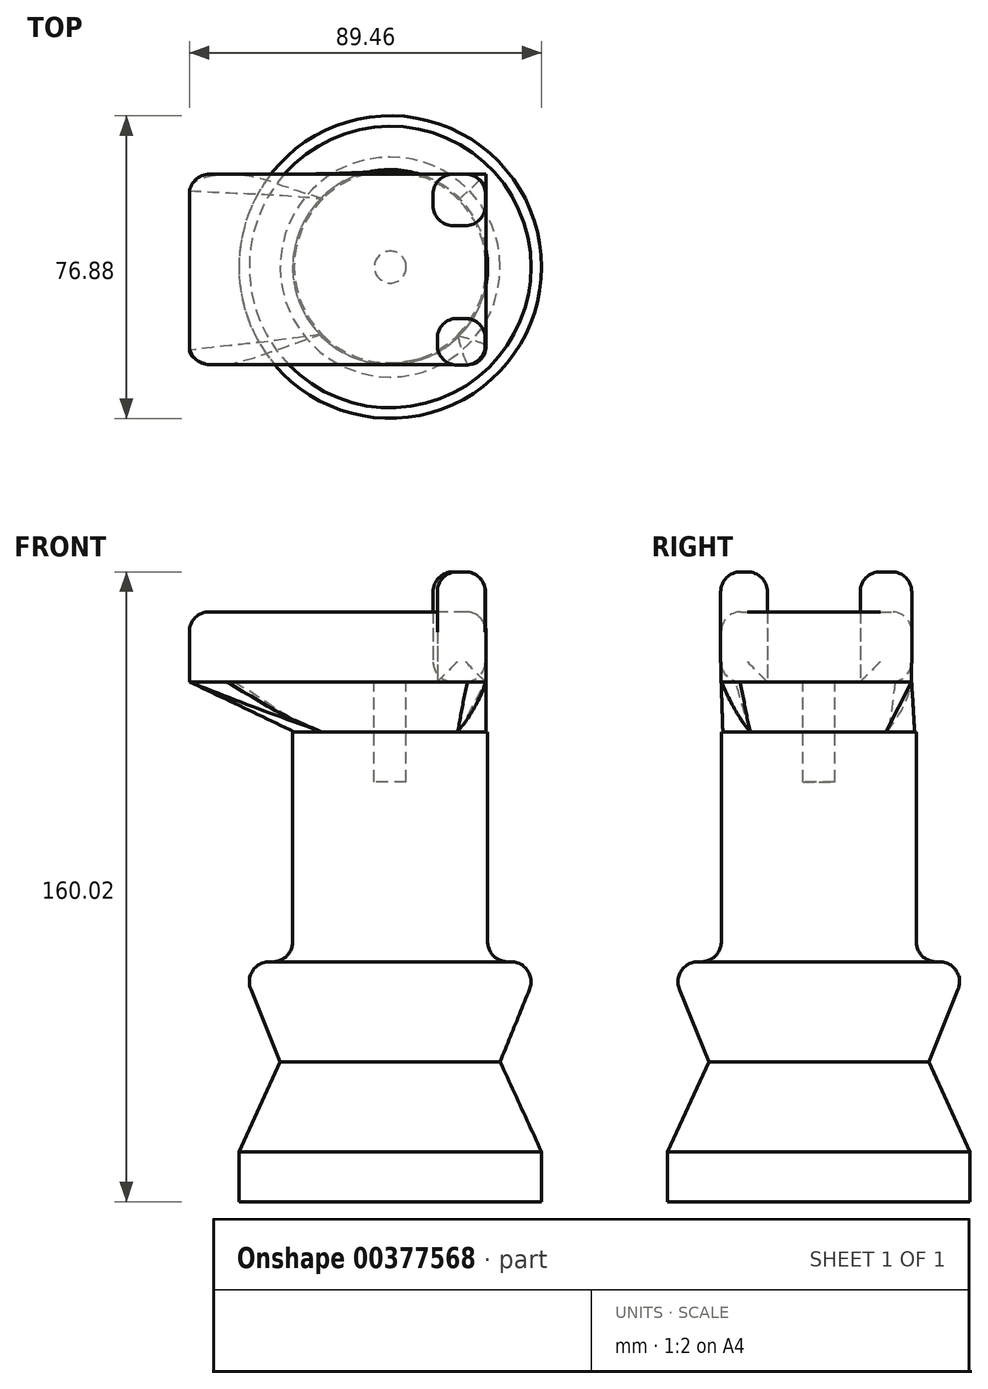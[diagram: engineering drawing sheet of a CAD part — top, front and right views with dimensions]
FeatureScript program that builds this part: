
annotation { "Feature Type Name" : "Feature", "Feature Type Description" : "" }
export const myFeature = defineFeature(function(context is Context, id is Id, definition is map)
    precondition{}
    {
        {
            var Q0;
            Q0=qCreatedBy(makeId("Top.planeOp"),FACE);
            var sketch = newSketch(context, id + "F0", { "sketchPlane" : qUnion([Q0])});
            skCircle(sketch, "E0", {"center": v(0, 0) * mm, "radius": 38.44 * mm});
            skSolve(sketch);
        }
        {
            var Q0;
            Q0=makeQuery(id+"F0.imprint","IMPRINT",FACE,{"disambiguationData":[TD([[makeQuery(id+"F0.imprint","IMPRINT",EDGE,{"derivedFrom":sQuery(id+"F0.wireOp",EDGE,"E0")}),1.0]])]});
            extrude(context, id + "F1", {"entities" : qUnion([Q0]), "oppositeDirection" : true, "depth" : 12.7 * mm});
        }
        {
            var Q0;
            Q0=qCreatedBy(makeId("Top.planeOp"),FACE);
            cPlane(context, id + "F2", {"entities" : qUnion([Q0]), "cplaneType" : CPlaneType.OFFSET, "offset" : 22.86 * mm, "width" : 152.4 * mm, "height" : 152.4 * mm});
        }
        {
            var Q0;
            Q0=qCreatedBy(id+"F2.planeOp",FACE);
            var sketch = newSketch(context, id + "F3", { "sketchPlane" : qUnion([Q0])});
            skCircle(sketch, "E1", {"center": v(0, 0) * mm, "radius": 27.93 * mm});
            skSolve(sketch);
        }
        {
            var Q1;
            Q1=makeQuery(id+"F0.imprint","IMPRINT",FACE,{"disambiguationData":[TD([[makeQuery(id+"F0.imprint","IMPRINT",EDGE,{"derivedFrom":sQuery(id+"F0.wireOp",EDGE,"E0")}),1.0]])]});
            var Q2;
            Q2=makeQuery(id+"F3.imprint","IMPRINT",FACE,{"disambiguationData":[TD([[makeQuery(id+"F3.imprint","IMPRINT",EDGE,{"derivedFrom":sQuery(id+"F3.wireOp",EDGE,"E1")}),1.0]])]});
            loft(context, id + "F4", {"operationType" : NewBodyOperationType.ADD, "sheetProfilesArray" : [{ "sheetProfileEntities" : qUnion([Q1]) }, { "sheetProfileEntities" : qUnion([Q2]) }]});
        }
        {
            var Q0;
            Q0=qCreatedBy(id+"F2.planeOp",FACE);
            cPlane(context, id + "F5", {"entities" : qUnion([Q0]), "cplaneType" : CPlaneType.OFFSET, "offset" : 25.4 * mm, "width" : 152.4 * mm, "height" : 152.4 * mm});
        }
        {
            var Q0;
            Q0=qCreatedBy(id+"F5.planeOp",FACE);
            var sketch = newSketch(context, id + "F6", { "sketchPlane" : qUnion([Q0])});
            skCircle(sketch, "E2", {"center": v(0, 0) * mm, "radius": 38.24 * mm});
            skSolve(sketch);
        }
        {
            var Q1;
            Q1 = qSketchRegion(id + "F6", true);
            var Q2;
            Q2=makeQuery(id+"F4.opLoft","CAP_FACE",FACE,{"disambiguationData":[OSD([makeQuery(id+"F3.imprint","IMPRINT",FACE,{"disambiguationData":[TD([[makeQuery(id+"F3.imprint","IMPRINT",EDGE,{"derivedFrom":sQuery(id+"F3.wireOp",EDGE,"E1")}),1.0]])]})])],"isStart":true});
            loft(context, id + "F7", {"operationType" : NewBodyOperationType.ADD, "sheetProfilesArray" : [{ "sheetProfileEntities" : qUnion([Q1]) }, { "sheetProfileEntities" : qUnion([Q2]) }]});
        }
        {
            var Q0;
            Q0=makeQuery(id+"F6.imprint","IMPRINT",FACE,{"disambiguationData":[TD([[makeQuery(id+"F6.imprint","IMPRINT",EDGE,{"derivedFrom":sQuery(id+"F6.wireOp",EDGE,"E2")}),1.0]])]});
            var sketch = newSketch(context, id + "F8", { "sketchPlane" : qUnion([Q0])});
            skCircle(sketch, "E3", {"center": v(0, 0) * mm, "radius": 24.77 * mm});
            skSolve(sketch);
        }
        {
            var Q0;
            Q0 = qSketchRegion(id + "F8", true);
            extrude(context, id + "F9", {"entities" : qUnion([Q0]), "operationType" : NewBodyOperationType.ADD, "depth" : 58.42 * mm});
        }
        {
            var Q0;
            Q0=qCreatedBy(id+"F5.planeOp",FACE);
            cPlane(context, id + "F10", {"entities" : qUnion([Q0]), "cplaneType" : CPlaneType.OFFSET, "offset" : 58.42 * mm, "width" : 152.4 * mm, "height" : 152.4 * mm});
        }
        {
            var Q0;
            Q0=makeQuery(id+"F9.opExtrude","CAP_FACE",FACE,{"disambiguationData":[OSD([sQuery(id+"F8.wireOp",EDGE,"E3")])],"isStart":false});
            var sketch = newSketch(context, id + "F11", { "sketchPlane" : qUnion([Q0])});
            skCircle(sketch, "E4", {"center": v(0, 0) * mm, "radius": 24.37 * mm});
            skSolve(sketch);
        }
        {
            var Q0;
            Q0=qCreatedBy(id+"F10.planeOp",FACE);
            cPlane(context, id + "F12", {"entities" : qUnion([Q0]), "cplaneType" : CPlaneType.OFFSET, "offset" : 12.7 * mm, "width" : 152.4 * mm, "height" : 152.4 * mm});
        }
        {
            var Q0;
            Q0=qCreatedBy(id+"F12.planeOp",FACE);
            var sketch = newSketch(context, id + "F13", { "sketchPlane" : qUnion([Q0])});
            skCircle(sketch, "E5", {"center": v(0, 0) * mm, "radius": 4.05 * mm});
            skSolve(sketch);
        }
        {
            var Q0;
            Q0=makeQuery(id+"F13.imprint","IMPRINT",FACE,{"disambiguationData":[TD([[makeQuery(id+"F13.imprint","IMPRINT",EDGE,{"derivedFrom":sQuery(id+"F13.wireOp",EDGE,"E5")}),1.0]])]});
            extrude(context, id + "F14", {"entities" : qUnion([Q0]), "oppositeDirection" : true, "depth" : 25.4 * mm});
        }
        {
            var Q0;
            Q0=qCreatedBy(id+"F12.planeOp",FACE);
            var sketch = newSketch(context, id + "F15", { "sketchPlane" : qUnion([Q0])});
            skLineSegment(sketch, "E6.bottom", {"start": v(24.35, -24.8) * mm, "end": v(-51.02, -24.8) * mm});
            skLineSegment(sketch, "E6.top", {"start": v(24.35, 23.59) * mm, "end": v(-51.02, 23.59) * mm});
            skLineSegment(sketch, "E6.left", {"start": v(24.35, -24.8) * mm, "end": v(24.35, 23.59) * mm});
            skLineSegment(sketch, "E6.right", {"start": v(-51.02, -24.8) * mm, "end": v(-51.02, 23.59) * mm});
            skSolve(sketch);
        }
        {
            var Q0;
            Q0 = qSketchRegion(id + "F11", true);
            var Q1;
            Q1 = qSketchRegion(id + "F15", true);
            loft(context, id + "F16", {"sheetProfilesArray" : [{ "sheetProfileEntities" : qUnion([Q0]) }, { "sheetProfileEntities" : qUnion([Q1]) }]});
        }
        {
            var Q0;
            Q0=makeQuery(id+"F15.imprint","IMPRINT",FACE,{"disambiguationData":[TD([[makeQuery(id+"F15.imprint","IMPRINT",EDGE,{"derivedFrom":sQuery(id+"F15.wireOp",EDGE,"E6.bottom")}),-1.0]])]});
            extrude(context, id + "F17", {"entities" : qUnion([Q0]), "depth" : 17.78 * mm});
        }
        {
            var Q0;
            Q0=qCreatedBy(id+"F12.planeOp",FACE);
            cPlane(context, id + "F18", {"entities" : qUnion([Q0]), "cplaneType" : CPlaneType.OFFSET, "offset" : 7.62 * mm, "width" : 152.4 * mm, "height" : 152.4 * mm});
        }
        {
            var Q0;
            Q0=qCreatedBy(id+"F18.planeOp",FACE);
            cPlane(context, id + "F19", {"entities" : qUnion([Q0]), "cplaneType" : CPlaneType.OFFSET, "offset" : 2.54 * mm, "width" : 152.4 * mm, "height" : 152.4 * mm});
        }
        {
            var Q0;
            Q0 = qSketchRegion(id + "F13", true);
            var sketch = newSketch(context, id + "F20", { "sketchPlane" : qUnion([Q0])});
            skLineSegment(sketch, "E7.bottom", {"start": v(24.14, -24.91) * mm, "end": v(11.96, -24.91) * mm});
            skLineSegment(sketch, "E7.top", {"start": v(24.14, -13.06) * mm, "end": v(11.96, -13.06) * mm});
            skLineSegment(sketch, "E7.left", {"start": v(24.14, -24.91) * mm, "end": v(24.14, -13.06) * mm});
            skLineSegment(sketch, "E7.right", {"start": v(11.96, -24.91) * mm, "end": v(11.96, -13.06) * mm});
            skLineSegment(sketch, "E8.bottom", {"start": v(24.22, 23.61) * mm, "end": v(10.91, 23.61) * mm});
            skLineSegment(sketch, "E8.top", {"start": v(24.22, 10.53) * mm, "end": v(10.91, 10.53) * mm});
            skLineSegment(sketch, "E8.left", {"start": v(24.22, 23.61) * mm, "end": v(24.22, 10.53) * mm});
            skLineSegment(sketch, "E8.right", {"start": v(10.91, 23.61) * mm, "end": v(10.91, 10.53) * mm});
            skLineSegment(sketch, "E9.bottom", {"start": v(11.96, -13.06) * mm, "end": v(24.14, -13.06) * mm});
            skLineSegment(sketch, "E9.top", {"start": v(11.96, -13.06) * mm, "end": v(24.14, -13.06) * mm});
            skLineSegment(sketch, "E9.left", {"start": v(11.96, -13.06) * mm, "end": v(11.96, -13.06) * mm});
            skLineSegment(sketch, "E9.right", {"start": v(24.14, -13.06) * mm, "end": v(24.14, -13.06) * mm});
            skSolve(sketch);
        }
        {
            var Q0;
            Q0 = qSketchRegion(id + "F20", true);
            extrude(context, id + "F21", {"entities" : qUnion([Q0]), "depth" : 27.94 * mm});
        }
        {
            var Q0;
            Q0=makeQuery(id+"F17.opExtrude","SWEPT_EDGE",EDGE,{"disambiguationData":[OSD([sQuery(id+"F15.wireOp",EDGE,"E6.top"),sQuery(id+"F15.wireOp",EDGE,"E6.right")])]});
            fillet(context, id + "F22", {"entities" : qUnion([Q0]), "radius" : 5.08 * mm, "tangentPropagation" : true, "allowEdgeOverflow" : false});
        }
        {
            var Q0;
            Q0=makeQuery(id+"F17.opExtrude","SWEPT_EDGE",EDGE,{"disambiguationData":[OSD([sQuery(id+"F15.wireOp",EDGE,"E6.bottom"),sQuery(id+"F15.wireOp",EDGE,"E6.right")])]});
            var Q1;
            Q1=makeQuery(id+"F16.opLoft","SWEPT_EDGE",EDGE,{"disambiguationData":[OSD([sQuery(id+"F11.wireOp",EDGE,"E4"),sQuery(id+"F15.wireOp",EDGE,"E6.bottom"),sQuery(id+"F15.wireOp",EDGE,"E6.top"),sQuery(id+"F15.wireOp",EDGE,"E6.right")])]});
            var Q2;
            Q2=makeQuery(id+"F16.opLoft","SWEPT_EDGE",EDGE,{"disambiguationData":[OSD([sQuery(id+"F11.wireOp",EDGE,"E4"),sQuery(id+"F15.wireOp",EDGE,"E6.top"),sQuery(id+"F15.wireOp",EDGE,"E6.left"),sQuery(id+"F15.wireOp",EDGE,"E6.right")])]});
            fillet(context, id + "F23", {"entities" : qUnion([Q0, Q1, Q2]), "radius" : 5.08 * mm, "tangentPropagation" : true, "allowEdgeOverflow" : false});
        }
        {
            var Q0;
            Q0=makeQuery(id+"F7.opLoft","CAP_FACE",FACE,{"disambiguationData":[OSD([makeQuery(id+"F6.imprint","IMPRINT",FACE,{"disambiguationData":[TD([[makeQuery(id+"F6.imprint","IMPRINT",EDGE,{"derivedFrom":sQuery(id+"F6.wireOp",EDGE,"E2")}),1.0]])]})])],"isStart":true});
            var Q1;
            Q1=makeQuery(id+"F17.opExtrude","SWEPT_EDGE",EDGE,{"disambiguationData":[OSD([sQuery(id+"F15.wireOp",EDGE,"E6.top"),sQuery(id+"F15.wireOp",EDGE,"E6.left")])]});
            var Q2;
            Q2=makeQuery(id+"F17.opExtrude","SWEPT_EDGE",EDGE,{"disambiguationData":[OSD([sQuery(id+"F15.wireOp",EDGE,"E6.bottom"),sQuery(id+"F15.wireOp",EDGE,"E6.left")])]});
            var Q3;
            Q3=makeQuery(id+"F16.opLoft","SWEPT_EDGE",EDGE,{"disambiguationData":[OSD([sQuery(id+"F11.wireOp",EDGE,"E4"),sQuery(id+"F15.wireOp",EDGE,"E6.bottom"),sQuery(id+"F15.wireOp",EDGE,"E6.top"),sQuery(id+"F15.wireOp",EDGE,"E6.left")])]});
            var Q4;
            Q4=makeQuery(id+"F16.opLoft","SWEPT_EDGE",EDGE,{"disambiguationData":[OSD([sQuery(id+"F15.wireOp",EDGE,"E6.bottom"),sQuery(id+"F15.wireOp",EDGE,"E6.left")])]});
            fillet(context, id + "F24", {"entities" : qUnion([Q0, Q1, Q2, Q3, Q4]), "radius" : 5.08 * mm, "tangentPropagation" : true, "allowEdgeOverflow" : false});
        }
        {
            var Q0;
            Q0=makeQuery(id+"F21.opExtrude","CAP_EDGE",EDGE,{"disambiguationData":[OSD([sQuery(id+"F20.wireOp",EDGE,"E8.bottom")])],"isStart":false});
            var Q1;
            Q1=makeQuery(id+"F21.opExtrude","SWEPT_FACE",FACE,{"disambiguationData":[OSD([sQuery(id+"F20.wireOp",EDGE,"E8.bottom")])]});
            var Q2;
            Q2=makeQuery(id+"F21.opExtrude","CAP_EDGE",EDGE,{"disambiguationData":[OSD([sQuery(id+"F20.wireOp",EDGE,"E7.bottom")])],"isStart":false});
            var Q3;
            Q3=makeQuery(id+"F21.opExtrude","SWEPT_FACE",FACE,{"disambiguationData":[OSD([sQuery(id+"F20.wireOp",EDGE,"E7.bottom")])]});
            var Q4;
            Q4=makeQuery(id+"F21.opExtrude","CAP_EDGE",EDGE,{"disambiguationData":[OSD([sQuery(id+"F20.wireOp",EDGE,"E8.top")])],"isStart":false});
            var Q5;
            Q5=makeQuery(id+"F21.opExtrude","CAP_EDGE",EDGE,{"disambiguationData":[OSD([sQuery(id+"F20.wireOp",EDGE,"E7.top")])],"isStart":false});
            var Q6;
            Q6=makeQuery(id+"F21.opExtrude","SWEPT_FACE",FACE,{"disambiguationData":[OSD([sQuery(id+"F20.wireOp",EDGE,"E8.right")])]});
            var Q7;
            Q7=makeQuery(id+"F21.opExtrude","SWEPT_FACE",FACE,{"disambiguationData":[OSD([sQuery(id+"F20.wireOp",EDGE,"E7.left")])]});
            var Q8;
            Q8=makeQuery(id+"F21.opExtrude","SWEPT_EDGE",EDGE,{"disambiguationData":[OSD([sQuery(id+"F20.wireOp",EDGE,"E7.right"),sQuery(id+"F20.wireOp",EDGE,"E7.top")])]});
            var Q9;
            Q9=makeQuery(id+"F21.opExtrude","CAP_EDGE",EDGE,{"disambiguationData":[OSD([sQuery(id+"F20.wireOp",EDGE,"E7.right")])],"isStart":false});
            var Q10;
            Q10=makeQuery(id+"F21.opExtrude","CAP_EDGE",EDGE,{"disambiguationData":[OSD([sQuery(id+"F20.wireOp",EDGE,"E8.left")])],"isStart":false});
            var Q11;
            Q11=makeQuery(id+"F21.opExtrude","SWEPT_EDGE",EDGE,{"disambiguationData":[OSD([sQuery(id+"F20.wireOp",EDGE,"E8.top"),sQuery(id+"F20.wireOp",EDGE,"E8.left")])]});
            var Q12;
            {var subQ0=sQuery(id+"F15.wireOp",EDGE,"E6.right");var subQ1=sQuery(id+"F15.wireOp",EDGE,"E6.top");Q12=makeQuery(id+"F22.opFillet","BLEND_EDGE",EDGE,{"blendedFrom":[makeQuery(id+"F17.opExtrude","SWEPT_EDGE",EDGE,{"disambiguationData":[OSD([subQ1,subQ0])]}),makeQuery(id+"F17.opExtrude","CAP_FACE",FACE,{"disambiguationData":[OSD([sQuery(id+"F15.wireOp",EDGE,"E6.bottom"),subQ1,sQuery(id+"F15.wireOp",EDGE,"E6.left"),subQ0])],"isStart":false})],"blendedInto":[makeQuery(id+"F17.opExtrude","CAP_FACE",FACE,{"disambiguationData":[OSD([sQuery(id+"F15.wireOp",EDGE,"E6.bottom"),subQ1,sQuery(id+"F15.wireOp",EDGE,"E6.left"),subQ0])],"isStart":false})]});}
            fillet(context, id + "F25", {"entities" : qUnion([Q0, Q1, Q2, Q3, Q4, Q5, Q6, Q7, Q8, Q9, Q10, Q11, Q12]), "radius" : 5.08 * mm, "tangentPropagation" : true, "allowEdgeOverflow" : false});
        }
    });
